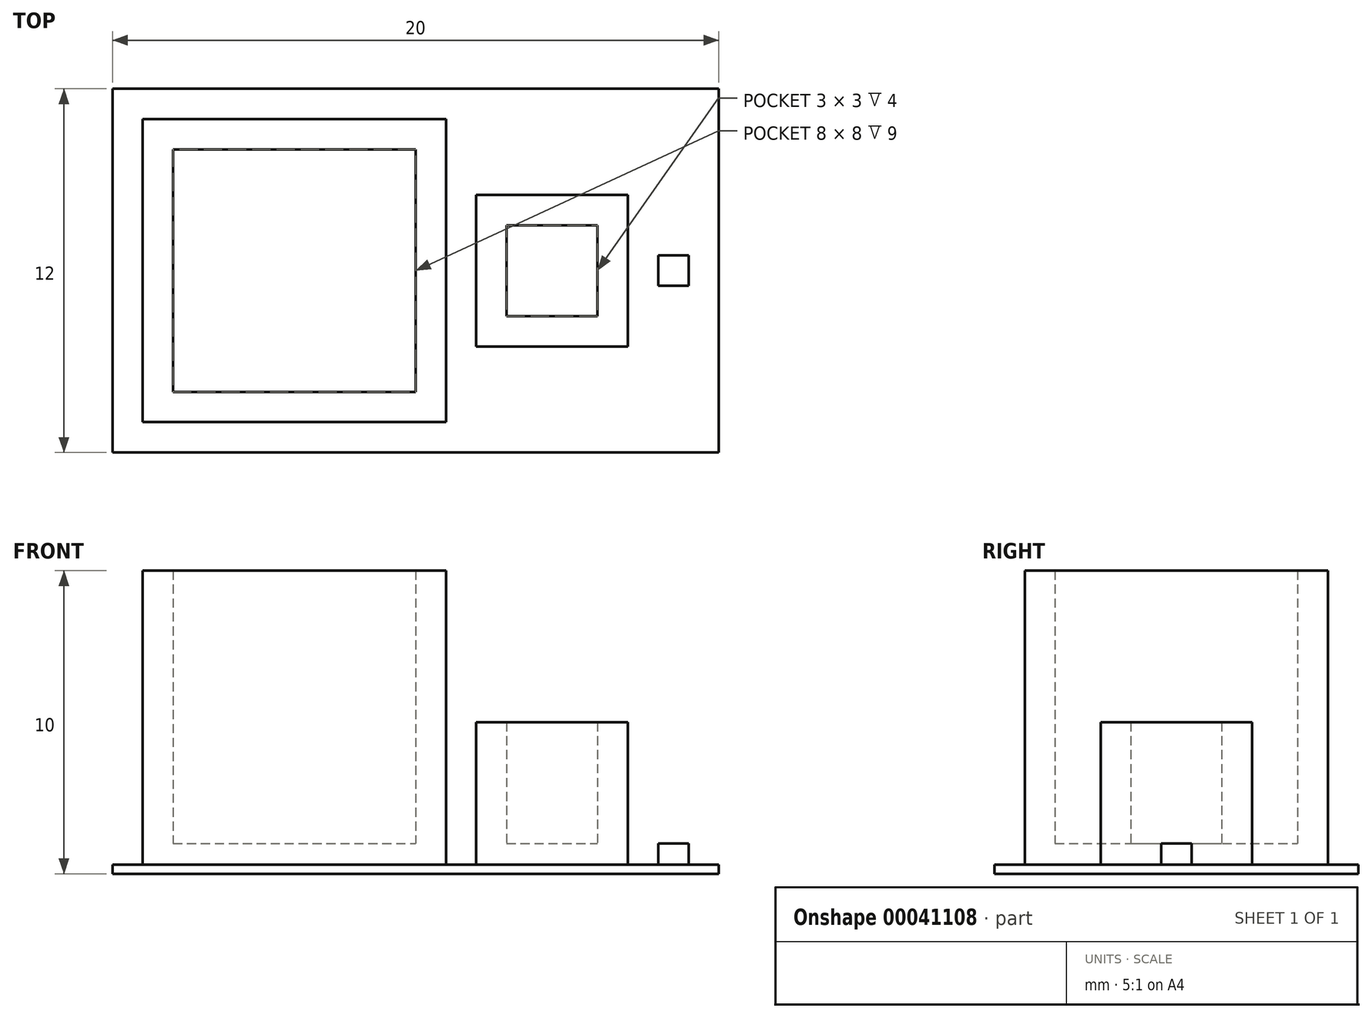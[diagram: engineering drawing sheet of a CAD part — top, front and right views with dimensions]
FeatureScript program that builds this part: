
annotation { "Feature Type Name" : "Feature", "Feature Type Description" : "" }
export const myFeature = defineFeature(function(context is Context, id is Id, definition is map)
    precondition{}
    {
        {
            var Q0;
            Q0=qCreatedBy(makeId("Top.planeOp"),FACE);
            var sketch = newSketch(context, id + "F0", { "sketchPlane" : qUnion([Q0])});
            skLineSegment(sketch, "E0.bottom", {"start": v(5, 5) * mm, "end": v(-5, 5) * mm});
            skLineSegment(sketch, "E0.top", {"start": v(5, -5) * mm, "end": v(-5, -5) * mm});
            skLineSegment(sketch, "E0.left", {"start": v(5, 5) * mm, "end": v(5, -5) * mm});
            skLineSegment(sketch, "E0.right", {"start": v(-5, 5) * mm, "end": v(-5, -5) * mm});
            skPoint(sketch, "E0.middle", {"position": v(0, 0) * mm});
            skLineSegment(sketch, "E1.bottom", {"start": v(11, 2.5) * mm, "end": v(6, 2.5) * mm});
            skLineSegment(sketch, "E1.top", {"start": v(11, -2.5) * mm, "end": v(6, -2.5) * mm});
            skLineSegment(sketch, "E1.left", {"start": v(11, 2.5) * mm, "end": v(11, -2.5) * mm});
            skLineSegment(sketch, "E1.right", {"start": v(6, 2.5) * mm, "end": v(6, -2.5) * mm});
            skPoint(sketch, "E1.middle", {"position": v(8.5, 0) * mm});
            skLineSegment(sketch, "E2.bottom", {"start": v(13, 0.5) * mm, "end": v(12, 0.5) * mm});
            skLineSegment(sketch, "E2.top", {"start": v(13, -0.5) * mm, "end": v(12, -0.5) * mm});
            skLineSegment(sketch, "E2.left", {"start": v(13, 0.5) * mm, "end": v(13, -0.5) * mm});
            skLineSegment(sketch, "E2.right", {"start": v(12, 0.5) * mm, "end": v(12, -0.5) * mm});
            skPoint(sketch, "E2.middle", {"position": v(12.5, 0) * mm});
            skLineSegment(sketch, "E3", {"start": v(-6, 6) * mm, "end": v(-6, -6) * mm});
            skLineSegment(sketch, "E4", {"start": v(-6, -6) * mm, "end": v(14, -6) * mm});
            skLineSegment(sketch, "E5", {"start": v(14, -6) * mm, "end": v(14, 6) * mm});
            skLineSegment(sketch, "E6", {"start": v(14, 6) * mm, "end": v(-6, 6) * mm});
            skSolve(sketch);
        }
        {
            var Q0;
            Q0=makeQuery(id+"F0.imprint","IMPRINT",FACE,{"disambiguationData":[TD([[makeQuery(id+"F0.imprint","IMPRINT",EDGE,{"derivedFrom":sQuery(id+"F0.wireOp",EDGE,"E0.bottom")}),1.0]])]});
            extrude(context, id + "F1", {"entities" : qUnion([Q0]), "depth" : 10 * mm});
        }
        {
            var Q0;
            Q0=makeQuery(id+"F0.imprint","IMPRINT",FACE,{"disambiguationData":[TD([[makeQuery(id+"F0.imprint","IMPRINT",EDGE,{"derivedFrom":sQuery(id+"F0.wireOp",EDGE,"E1.bottom")}),1.0]])]});
            extrude(context, id + "F2", {"entities" : qUnion([Q0]), "depth" : 5 * mm});
        }
        {
            var Q0;
            Q0=makeQuery(id+"F0.imprint","IMPRINT",FACE,{"disambiguationData":[TD([[makeQuery(id+"F0.imprint","IMPRINT",EDGE,{"derivedFrom":sQuery(id+"F0.wireOp",EDGE,"E2.bottom")}),1.0]])]});
            extrude(context, id + "F3", {"entities" : qUnion([Q0]), "depth" : 1 * mm});
        }
        {
            var Q0;
            Q0=makeQuery(id+"F0.imprint","IMPRINT",FACE,{"disambiguationData":[TD([[makeQuery(id+"F0.imprint","IMPRINT",EDGE,{"derivedFrom":sQuery(id+"F0.wireOp",EDGE,"E0.bottom")}),-1.0]])]});
            extrude(context, id + "F4", {"entities" : qUnion([Q0]), "operationType" : NewBodyOperationType.ADD, "depth" : .3 * mm});
        }
        {
            var Q0;
            Q0=makeQuery(id+"F1.opExtrude","CAP_FACE",FACE,{"disambiguationData":[OSD([sQuery(id+"F0.wireOp",EDGE,"E0.bottom"),sQuery(id+"F0.wireOp",EDGE,"E0.top"),sQuery(id+"F0.wireOp",EDGE,"E0.left"),sQuery(id+"F0.wireOp",EDGE,"E0.right")])],"isStart":false});
            var Q1;
            Q1=makeQuery(id+"F2.opExtrude","CAP_FACE",FACE,{"disambiguationData":[OSD([sQuery(id+"F0.wireOp",EDGE,"E1.bottom"),sQuery(id+"F0.wireOp",EDGE,"E1.top"),sQuery(id+"F0.wireOp",EDGE,"E1.left"),sQuery(id+"F0.wireOp",EDGE,"E1.right")])],"isStart":false});
            var Q2;
            Q2=makeQuery(id+"F3.opExtrude","CAP_FACE",FACE,{"disambiguationData":[OSD([sQuery(id+"F0.wireOp",EDGE,"E2.bottom"),sQuery(id+"F0.wireOp",EDGE,"E2.top"),sQuery(id+"F0.wireOp",EDGE,"E2.left"),sQuery(id+"F0.wireOp",EDGE,"E2.right")])],"isStart":false});
            shell(context, id + "F5", {"entities" : qUnion([Q0, Q1, Q2]), "thickness" : 1 * mm});
        }
    });
